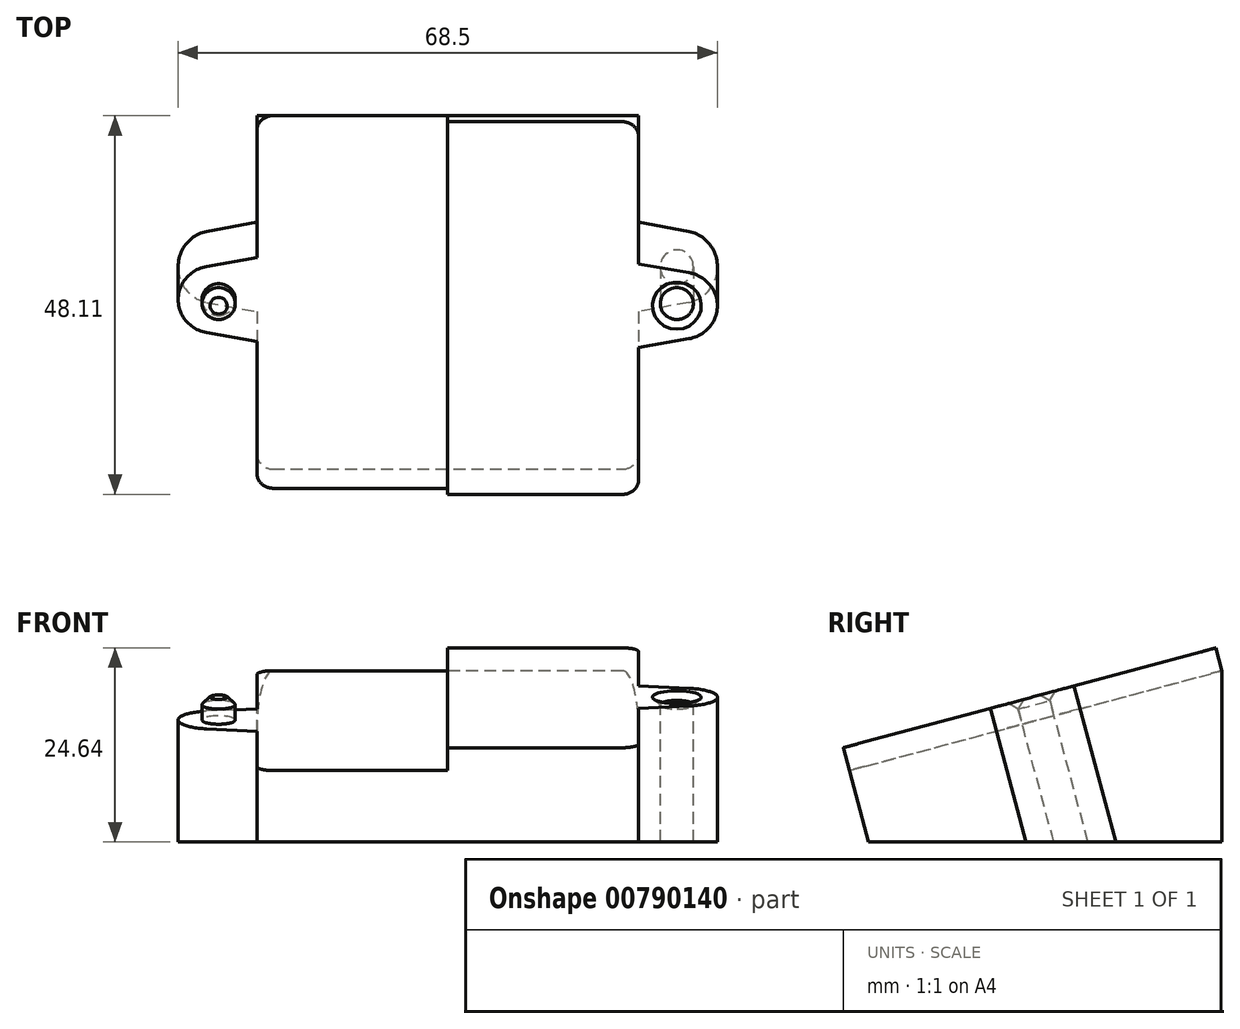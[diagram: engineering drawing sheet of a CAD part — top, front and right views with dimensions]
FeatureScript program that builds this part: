
annotation { "Feature Type Name" : "Feature", "Feature Type Description" : "" }
export const myFeature = defineFeature(function(context is Context, id is Id, definition is map)
    precondition{}
    {
        {
            var Q0;
            Q0=qCreatedBy(makeId("Right.planeOp"),FACE);
            var sketch = newSketch(context, id + "F0", { "sketchPlane" : qUnion([Q0])});
            skLineSegment(sketch, "E0", {"start": v(0, 0) * mm, "end": v(81.14, 0) * mm});
            skLineSegment(sketch, "E1", {"start": v(81.14, 0) * mm, "end": v(81.14, 21.74) * mm});
            skLineSegment(sketch, "E2", {"start": v(81.14, 21.74) * mm, "end": v(0, 0) * mm});
            skSolve(sketch);
        }
        {
            var Q0;
            Q0=makeQuery(id+"F0.imprint","IMPRINT",FACE,{"disambiguationData":[TD([[makeQuery(id+"F0.imprint","IMPRINT",EDGE,{"derivedFrom":sQuery(id+"F0.wireOp",EDGE,"E0")}),1.0]])]});
            extrude(context, id + "F1", {"entities" : qUnion([Q0]), "endBound" : BoundingType.SYMMETRIC, "depth" : 68.5 * mm, "offsetDistance" : 25 * mm});
        }
        {
            var Q0;
            Q0=makeQuery(id+"F1.opExtrude","SWEPT_FACE",FACE,{"disambiguationData":[OSD([sQuery(id+"F0.wireOp",EDGE,"E2")])]});
            var sketch = newSketch(context, id + "F2", { "sketchPlane" : qUnion([Q0])});
            skLineSegment(sketch, "E3.bottom", {"start": v(0, 35) * mm, "end": v(-22.25, 35) * mm});
            skLineSegment(sketch, "E3.top", {"start": v(0, 84) * mm, "end": v(-22.25, 84) * mm});
            skLineSegment(sketch, "E3.left", {"start": v(0, 35) * mm, "end": v(0, 84) * mm});
            skLineSegment(sketch, "E3.right", {"start": v(-24.25, 37) * mm, "end": v(-24.25, 54.32) * mm});
            skLineSegment(sketch, "E4", {"start": v(-24.25, 54.32) * mm, "end": v(-30.62, 55.47) * mm});
            skLineSegment(sketch, "E5.MirrorCS", {"start": v(-24.25, 65.32) * mm, "end": v(-30.62, 64.17) * mm});
            skLineSegment(sketch, "E6.trimOffspring", {"start": v(-24.25, 65.32) * mm, "end": v(-24.25, 82) * mm});
            skLineSegment(sketch, "E7.MirrorCS", {"start": v(24.25, 65.32) * mm, "end": v(30.62, 64.17) * mm});
            skLineSegment(sketch, "E8.MirrorCS", {"start": v(24.25, 37) * mm, "end": v(24.25, 54.32) * mm});
            skLineSegment(sketch, "E9.MirrorCS", {"start": v(24.25, 54.32) * mm, "end": v(30.62, 55.47) * mm});
            skLineSegment(sketch, "E10.MirrorCS", {"start": v(24.25, 65.32) * mm, "end": v(24.25, 82) * mm});
            skLineSegment(sketch, "E11.MirrorCS", {"start": v(0, 84) * mm, "end": v(22.25, 84) * mm});
            skLineSegment(sketch, "E12.MirrorCS", {"start": v(0, 35) * mm, "end": v(22.25, 35) * mm});
            skArc(sketch, "E13", {"start": v(-30.62, 64.17) * mm, "mid": v(-34.25, 59.82) * mm, "end": v(-30.62, 55.47) * mm});
            skPoint(sketch, "E13.third.point", {"position": v(-34.25, 59.82) * mm});
            skLineSegment(sketch, "E14", {"start": v(-24.25, 54.32) * mm, "end": v(-24.25, 65.32) * mm, "construction": true});
            skPoint(sketch, "E15.startSnap0", {"position": v(-24.25, 59.82) * mm});
            skLineSegment(sketch, "E16", {"start": v(-24.25, 59.82) * mm, "end": v(-34.25, 59.82) * mm, "construction": true});
            skCircle(sketch, "E17", {"center": v(-29.1, 59.82) * mm, "radius": 2.1 * mm});
            skCircle(sketch, "E18.MirrorC", {"center": v(29.1, 59.82) * mm, "radius": 2.1 * mm});
            skArc(sketch, "E19.MirrorCS", {"start": v(30.62, 64.17) * mm, "mid": v(34.25, 59.82) * mm, "end": v(30.62, 55.47) * mm});
            skLineSegment(sketch, "E20", {"start": v(-30.62, 55.47) * mm, "end": v(-30.62, 64.17) * mm, "construction": true});
            skPoint(sketch, "E21.visualSharp", {"position": v(-24.25, 35) * mm});
            skArc(sketch, "E21.filletArc", {"start": v(-24.25, 37) * mm, "mid": v(-23.66, 35.59) * mm, "end": v(-22.25, 35) * mm});
            skPoint(sketch, "E22.visualSharp", {"position": v(-24.25, 84) * mm});
            skArc(sketch, "E22.filletArc", {"start": v(-22.25, 84) * mm, "mid": v(-23.66, 83.41) * mm, "end": v(-24.25, 82) * mm});
            skPoint(sketch, "E23.visualSharp", {"position": v(24.25, 35) * mm});
            skArc(sketch, "E23.filletArc", {"start": v(22.25, 35) * mm, "mid": v(23.66, 35.59) * mm, "end": v(24.25, 37) * mm});
            skPoint(sketch, "E24.visualSharp", {"position": v(24.25, 84) * mm});
            skArc(sketch, "E24.filletArc", {"start": v(24.25, 82) * mm, "mid": v(23.66, 83.41) * mm, "end": v(22.25, 84) * mm});
            skSolve(sketch);
        }
        {
            var Q0;
            Q0 = qSketchRegion(id + "F2", true);
            var Q1;
            Q1=makeQuery(id+"F2.imprint","IMPRINT",FACE,{"disambiguationData":[TD([[makeQuery(id+"F2.imprint","IMPRINT",EDGE,{"derivedFrom":sQuery(id+"F2.wireOp",EDGE,"E18.MirrorC")}),-1.0]])]});
            var Q2;
            Q2=makeQuery(id+"F2.imprint","IMPRINT",FACE,{"disambiguationData":[TD([[makeQuery(id+"F2.imprint","IMPRINT",EDGE,{"derivedFrom":sQuery(id+"F2.wireOp",EDGE,"E17")}),1.0]])]});
            extrude(context, id + "F3", {"entities" : qUnion([Q0, Q1, Q2]), "depth" : -30 * mm, "offsetDistance" : 25 * mm});
        }
        {
            var Q0;
            Q0=makeQuery(id+"F3.opExtrude","SWEPT_BODY",BODY,{"disambiguationData":[OSD([sQuery(id+"F2.wireOp",EDGE,"E3.bottom"),sQuery(id+"F2.wireOp",EDGE,"E3.top"),sQuery(id+"F2.wireOp",EDGE,"E3.right"),sQuery(id+"F2.wireOp",EDGE,"E4"),sQuery(id+"F2.wireOp",EDGE,"E5.MirrorCS"),sQuery(id+"F2.wireOp",EDGE,"E6.trimOffspring"),sQuery(id+"F2.wireOp",EDGE,"E7.MirrorCS"),sQuery(id+"F2.wireOp",EDGE,"E8.MirrorCS"),sQuery(id+"F2.wireOp",EDGE,"E9.MirrorCS"),sQuery(id+"F2.wireOp",EDGE,"E10.MirrorCS"),sQuery(id+"F2.wireOp",EDGE,"E11.MirrorCS"),sQuery(id+"F2.wireOp",EDGE,"E12.MirrorCS"),sQuery(id+"F2.wireOp",EDGE,"E13"),sQuery(id+"F2.wireOp",EDGE,"E17"),sQuery(id+"F2.wireOp",EDGE,"E18.MirrorC"),sQuery(id+"F2.wireOp",EDGE,"E19.MirrorCS"),sQuery(id+"F2.wireOp",EDGE,"E21.filletArc"),sQuery(id+"F2.wireOp",EDGE,"E22.filletArc"),sQuery(id+"F2.wireOp",EDGE,"E23.filletArc"),sQuery(id+"F2.wireOp",EDGE,"E24.filletArc")])]});
            var Q1;
            Q1=makeQuery(id+"F1.opExtrude","SWEPT_BODY",BODY,{"disambiguationData":[OSD([sQuery(id+"F0.wireOp",EDGE,"E0"),sQuery(id+"F0.wireOp",EDGE,"E1"),sQuery(id+"F0.wireOp",EDGE,"E2")])]});
            booleanBodies(context, id + "F4", {"operationType" : BooleanOperationType.INTERSECTION, "tools" : qUnion([Q0, Q1])});
        }
        {
            var Q0;
            Q0=makeQuery(id+"F2.imprint","IMPRINT",FACE,{"disambiguationData":[TD([[makeQuery(id+"F2.imprint","IMPRINT",EDGE,{"derivedFrom":sQuery(id+"F2.wireOp",EDGE,"E18.MirrorC")}),-1.0]])]});
            var Q1;
            Q1=makeQuery(id+"F2.imprint","IMPRINT",FACE,{"disambiguationData":[TD([[makeQuery(id+"F2.imprint","IMPRINT",EDGE,{"derivedFrom":sQuery(id+"F2.wireOp",EDGE,"E17")}),1.0]])]});
            extrude(context, id + "F5", {"entities" : qUnion([Q0, Q1]), "operationType" : NewBodyOperationType.ADD, "depth" : 3 * mm, "offsetDistance" : 25 * mm});
        }
        {
            var Q0;
            Q0=makeQuery(id+"F5.opExtrude","CAP_EDGE",EDGE,{"disambiguationData":[OSD([sQuery(id+"F2.wireOp",EDGE,"E18.MirrorC")])],"isStart":false});
            var Q1;
            Q1=makeQuery(id+"F5.opExtrude","CAP_EDGE",EDGE,{"disambiguationData":[OSD([sQuery(id+"F2.wireOp",EDGE,"E17")])],"isStart":false});
            chamfer(context, id + "F6", {"entities" : qUnion([Q0, Q1]), "width" : 1 * mm});
        }
    });
